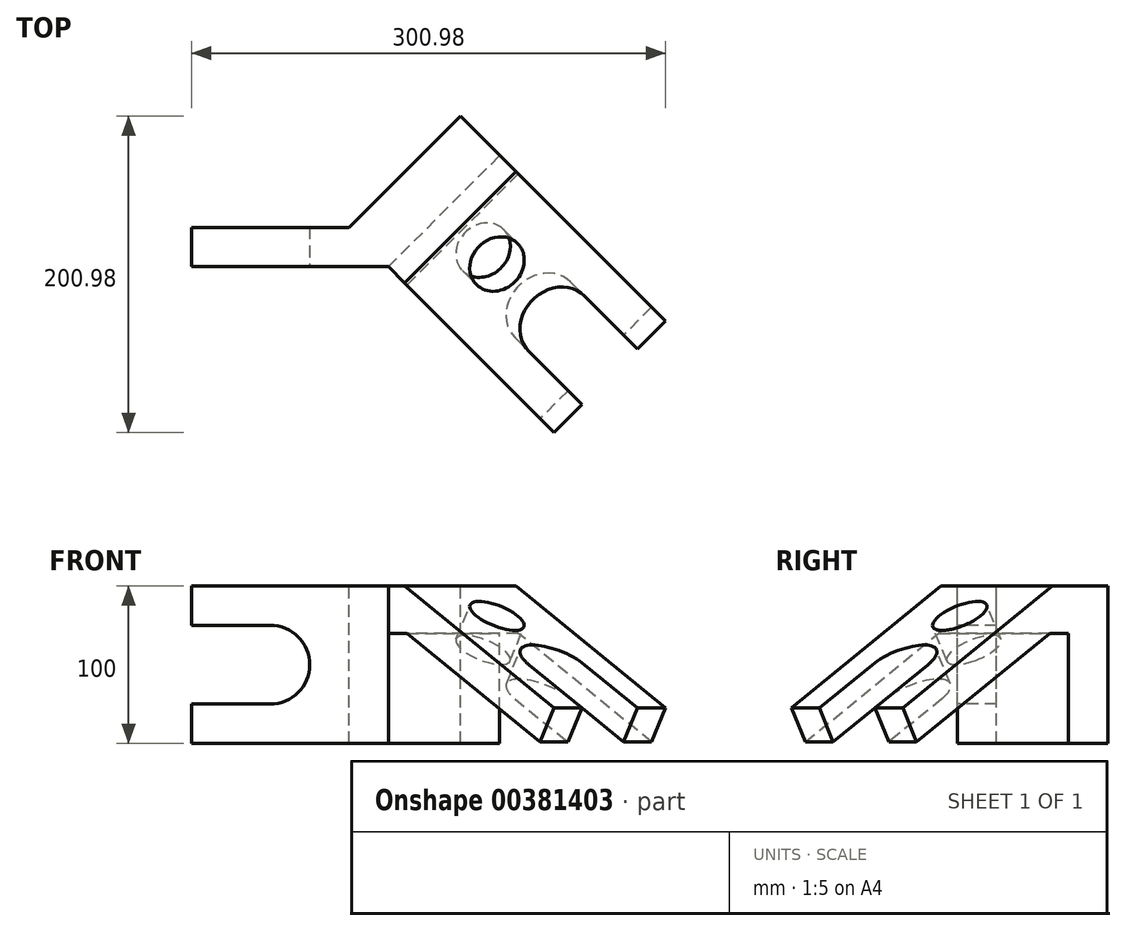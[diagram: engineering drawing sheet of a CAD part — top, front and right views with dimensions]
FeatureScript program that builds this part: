
annotation { "Feature Type Name" : "Feature", "Feature Type Description" : "" }
export const myFeature = defineFeature(function(context is Context, id is Id, definition is map)
    precondition{}
    {
        {
            var Q0;
            Q0=qCreatedBy(makeId("Top.planeOp"),FACE);
            var sketch = newSketch(context, id + "F0", { "sketchPlane" : qUnion([Q0])});
            skLineSegment(sketch, "E0", {"start": v(25, -25) * mm, "end": v(-100, -25) * mm});
            skLineSegment(sketch, "E1", {"start": v(-100, -25) * mm, "end": v(-100, 0) * mm});
            skLineSegment(sketch, "E2", {"start": v(-100, 0) * mm, "end": v(0, 0) * mm});
            skLineSegment(sketch, "E3", {"start": v(0, 0) * mm, "end": v(70.71, 70.71) * mm});
            skLineSegment(sketch, "E4", {"start": v(70.71, 70.71) * mm, "end": v(95.71, 45.71) * mm});
            skLineSegment(sketch, "E5", {"start": v(95.71, 45.71) * mm, "end": v(25, -25) * mm});
            skLineSegment(sketch, "E6", {"start": v(25, -25) * mm, "end": v(0, 0) * mm, "construction": true});
            skSolve(sketch);
        }
        {
            var Q0;
            Q0=qCreatedBy(makeId("Right.planeOp"),FACE);
            var sketch = newSketch(context, id + "F1", { "sketchPlane" : qUnion([Q0])});
            skLineSegment(sketch, "E7", {"start": v(72.83, -34.5) * mm, "end": v(72.83, -60.58) * mm});
            skLineSegment(sketch, "E8", {"start": v(72.83, -60.58) * mm, "end": v(24.8, -60.58) * mm});
            skLineSegment(sketch, "E9", {"start": v(24.8, -60.58) * mm, "end": v(-33.17, -125.62) * mm});
            skLineSegment(sketch, "E10", {"start": v(-33.17, -125.62) * mm, "end": v(-52.28, -108.59) * mm});
            skLineSegment(sketch, "E11", {"start": v(-52.28, -108.59) * mm, "end": v(13.77, -34.5) * mm});
            skLineSegment(sketch, "E12", {"start": v(13.77, -34.5) * mm, "end": v(72.83, -34.5) * mm});
            skLineSegment(sketch, "E13", {"start": v(0, 0) * mm, "end": v(0, 54.98) * mm});
            skSolve(sketch);
        }
        {
            var Q0;
            Q0=sQuery(id+"F0.wireOp",VERTEX,"E6.start");
            var Q1;
            Q1=sQuery(id+"F1.wireOp",VERTEX,"E13.start");
            var Q2;
            Q2=sQuery(id+"F1.wireOp",VERTEX,"E13.end");
            cPlane(context, id + "F2", {"entities" : qUnion([Q0, Q1, Q2]), "cplaneType" : CPlaneType.THREE_POINT, "offset" : 25 * mm, "width" : 150 * mm, "height" : 150 * mm});
        }
        {
            var Q0;
            Q0=qCreatedBy(id+"F2.planeOp",FACE);
            var sketch = newSketch(context, id + "F3", { "sketchPlane" : qUnion([Q0])});
            skLineSegment(sketch, "E14", {"start": v(0, -30) * mm, "end": v(0, 0) * mm});
            skLineSegment(sketch, "E15", {"start": v(0, 0) * mm, "end": v(50, 0) * mm});
            skLineSegment(sketch, "E16", {"start": v(50, 0) * mm, "end": v(184.23, -77.5) * mm});
            skLineSegment(sketch, "E17", {"start": v(184.23, -77.5) * mm, "end": v(171.73, -99.15) * mm});
            skLineSegment(sketch, "E18", {"start": v(171.73, -99.15) * mm, "end": v(51.96, -30) * mm});
            skLineSegment(sketch, "E19", {"start": v(51.96, -30) * mm, "end": v(0, -30) * mm});
            skSolve(sketch);
        }
        {
            var Q0;
            Q0=makeQuery(id+"F0.imprint","IMPRINT",FACE,{"disambiguationData":[TD([[makeQuery(id+"F0.imprint","IMPRINT",EDGE,{"derivedFrom":sQuery(id+"F0.wireOp",EDGE,"E0")}),-1.0]])]});
            extrude(context, id + "F4", {"entities" : qUnion([Q0]), "oppositeDirection" : true, "depth" : 100 * mm});
        }
        {
            var Q0;
            Q0=makeQuery(id+"F3.imprint","IMPRINT",FACE,{"disambiguationData":[TD([[makeQuery(id+"F3.imprint","IMPRINT",EDGE,{"derivedFrom":sQuery(id+"F3.wireOp",EDGE,"E14")}),-1.0]])]});
            extrude(context, id + "F5", {"entities" : qUnion([Q0]), "operationType" : NewBodyOperationType.ADD, "oppositeDirection" : true, "depth" : 100 * mm});
        }
        {
            var Q0;
            Q0=makeQuery(id+"F4.opExtrude","SWEPT_FACE",FACE,{"disambiguationData":[OSD([sQuery(id+"F0.wireOp",EDGE,"E0")])]});
            var sketch = newSketch(context, id + "F6", { "sketchPlane" : qUnion([Q0])});
            skLineSegment(sketch, "E20", {"start": v(-100, -25) * mm, "end": v(-50, -25) * mm});
            skLineSegment(sketch, "E21", {"start": v(-100, -75) * mm, "end": v(-50, -75) * mm});
            skArc(sketch, "E22", {"start": v(-50, -25) * mm, "mid": v(-25, -50) * mm, "end": v(-50, -75) * mm});
            skSolve(sketch);
        }
        {
            var Q0;
            {var subQ0=sQuery(id+"F6.wireOp",EDGE,"E20");Q0=makeQuery(id+"F6.imprint","IMPRINT",FACE,{"disambiguationData":[TD([[makeQuery(id+"F6.imprint","IMPRINT",EDGE,{"derivedFrom":subQ0}),-1.0]])]});}
            extrude(context, id + "F7", {"entities" : qUnion([Q0]), "operationType" : NewBodyOperationType.REMOVE, "endBound" : BoundingType.UP_TO_NEXT, "oppositeDirection" : true, "depth" : 25 * mm});
        }
        {
            var Q0;
            Q0=makeQuery(id+"F5.opExtrude","SWEPT_FACE",FACE,{"disambiguationData":[OSD([sQuery(id+"F3.wireOp",EDGE,"E16")])]});
            var sketch = newSketch(context, id + "F8", { "sketchPlane" : qUnion([Q0])});
            skCircle(sketch, "E23", {"center": v(91.02, -28.73) * mm, "radius": 18.5 * mm});
            skLineSegment(sketch, "E24", {"start": v(148.72, -133.54) * mm, "end": v(112.71, -91.96) * mm});
            skLineSegment(sketch, "E25", {"start": v(186.51, -100.8) * mm, "end": v(150.5, -59.23) * mm});
            skArc(sketch, "E26", {"start": v(150.5, -59.23) * mm, "mid": v(115.24, -56.7) * mm, "end": v(112.71, -91.96) * mm});
            skSolve(sketch);
        }
        {
            var Q0;
            Q0=makeQuery(id+"F8.imprint","IMPRINT",FACE,{"disambiguationData":[TD([[makeQuery(id+"F8.imprint","IMPRINT",EDGE,{"derivedFrom":sQuery(id+"F8.wireOp",EDGE,"E23")}),1.0]])]});
            var Q1;
            {var subQ0=sQuery(id+"F8.wireOp",EDGE,"E24");Q1=makeQuery(id+"F8.imprint","IMPRINT",FACE,{"disambiguationData":[TD([[makeQuery(id+"F8.imprint","IMPRINT",EDGE,{"derivedFrom":subQ0}),-1.0]])]});}
            extrude(context, id + "F9", {"entities" : qUnion([Q0, Q1]), "operationType" : NewBodyOperationType.REMOVE, "endBound" : BoundingType.UP_TO_NEXT, "oppositeDirection" : true, "depth" : 25 * mm});
        }
    });
